# Revit family: Heat_pump_MasterTherm_AQ17ICP_01
name_source: partatom
category: Mechanické zařízení
units: mm (PartAtom-declared; Revit-internal decimal feet)

## family parameters
Bod výpočtu místnosti = Ne
Klasifikace = Žádné
Kóta kulaté spojky = Použít průměr
Nadpis OmniClass = Climate Control (HVAC)
Ořezat dutým tvarem při načtení = Ne
Sdílené = Ne
Typ dílu = Normální
Vždy vertikální = Ano
Založené na pracovní rovině = Ne
Číslo OmniClass = 23.75.00.00

## types (1)
- Heat_pump_MasterTherm_AQ17ICP_01
    Brine inlet = 25 mm  [stored 0.082021 ft]
    Brine outlet = 25 mm  [stored 0.082021 ft]
    El. bushings 2xPG29 = 1
    Hot water inlet = 25 mm  [stored 0.082021 ft]
    Hot water outlet = 25 mm  [stored 0.082021 ft]
    Model = AQ17ICP
    Popis = Inverter, speed 15-90 rps; heating capacity 1-6 kW (B0W35); storage volume 150 l; voltage 1x230 V; Max. current 16 A; weight (operating) 105(260) kg; W/B overpressure 0,25 MPa; Ref. overpressure 3,1 MPa; brine Min/Max -5/+20 °C; water Min/Max 20/75 °C; refrigerant R290
    SHW inlet = 13 mm  [stored 0.0426509 ft]
    SHW outlet = 13 mm  [stored 0.0426509 ft]
    Voltage = 230 V
    Výchozí výška = 0 mm  [stored 0 ft]
    Výrobce = MasterTherm

note: [stored X ft] marks values corroborated as IEEE doubles in the binary element streams (Revit-internal decimal feet)

## geometry (parser evidence)
native form markers: Sweep x3
no freeform markers — native parametric forms only
